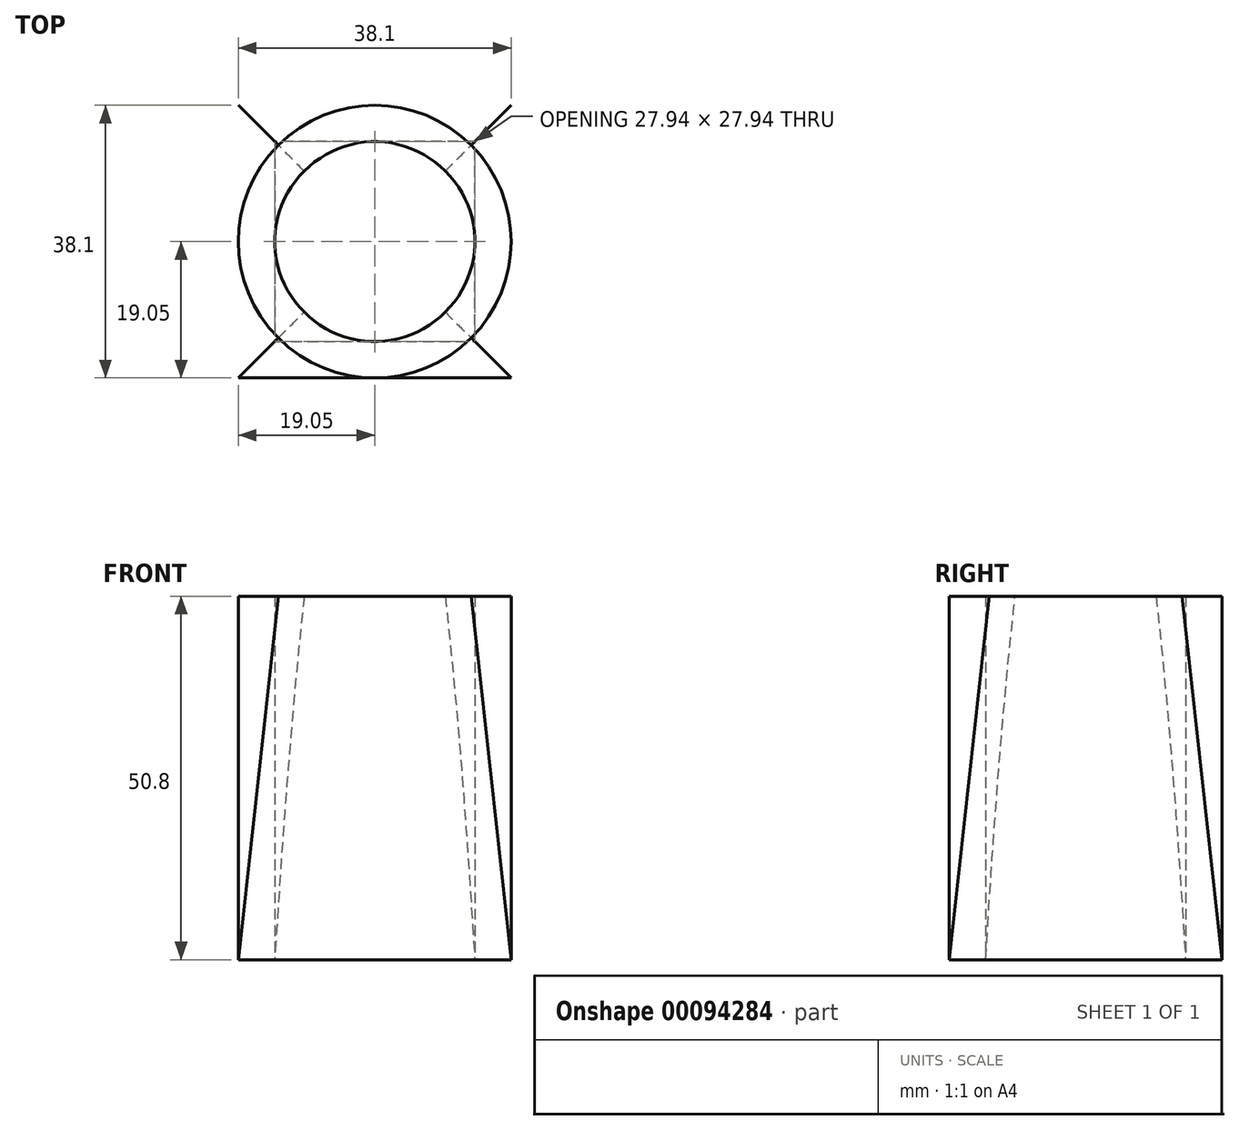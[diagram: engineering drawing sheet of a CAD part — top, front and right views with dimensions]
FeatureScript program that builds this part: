
annotation { "Feature Type Name" : "Feature", "Feature Type Description" : "" }
export const myFeature = defineFeature(function(context is Context, id is Id, definition is map)
    precondition{}
    {
        {
            var Q0;
            Q0=qCreatedBy(makeId("Front.planeOp"),FACE);
            var sketch = newSketch(context, id + "F0", { "sketchPlane" : qUnion([Q0])});
            skLineSegment(sketch, "E0", {"start": v(-19.05, 0) * mm, "end": v(-19.05, 50.8) * mm});
            skSolve(sketch);
        }
        {
            var Q0;
            Q0=qCreatedBy(makeId("Top.planeOp"),FACE);
            var sketch = newSketch(context, id + "F1", { "sketchPlane" : qUnion([Q0])});
            skLineSegment(sketch, "E1.bottom", {"start": v(-19.05, -19.05) * mm, "end": v(19.05, -19.05) * mm});
            skLineSegment(sketch, "E1.top", {"start": v(-19.05, 19.05) * mm, "end": v(19.05, 19.05) * mm});
            skLineSegment(sketch, "E1.left", {"start": v(-19.05, -19.05) * mm, "end": v(-19.05, 19.05) * mm});
            skLineSegment(sketch, "E1.right", {"start": v(19.05, -19.05) * mm, "end": v(19.05, 19.05) * mm});
            skPoint(sketch, "E1.middle", {"position": v(0, 0) * mm});
            skSolve(sketch);
        }
        {
            var Q0;
            Q0=sQuery(id+"F0.wireOp",VERTEX,"E0.end");
            var Q1;
            Q1=qCreatedBy(makeId("Top.planeOp"),FACE);
            cPlane(context, id + "F2", {"entities" : qUnion([Q0, Q1]), "cplaneType" : CPlaneType.PLANE_POINT, "offset" : 152.4 * mm, "width" : 152.4 * mm, "height" : 152.4 * mm});
        }
        {
            var Q0;
            Q0=qCreatedBy(id+"F2.planeOp",FACE);
            var sketch = newSketch(context, id + "F3", { "sketchPlane" : qUnion([Q0])});
            skCircle(sketch, "E2", {"center": v(0, 0) * mm, "radius": 19.05 * mm});
            skSolve(sketch);
        }
        {
            var Q0;
            Q0=makeQuery(id+"F1.imprint","IMPRINT",FACE,{"disambiguationData":[TD([[makeQuery(id+"F1.imprint","IMPRINT",EDGE,{"derivedFrom":sQuery(id+"F1.wireOp",EDGE,"E1.bottom")}),1.0]])]});
            var Q1;
            Q1=makeQuery(id+"F3.imprint","IMPRINT",FACE,{"disambiguationData":[TD([[makeQuery(id+"F3.imprint","IMPRINT",EDGE,{"derivedFrom":sQuery(id+"F3.wireOp",EDGE,"E2")}),1.0]])]});
            loft(context, id + "F4", {"sheetProfilesArray" : [{ "sheetProfileEntities" : qUnion([Q0]) }, { "sheetProfileEntities" : qUnion([Q1]) }]});
        }
        {
            var Q0;
            Q0=makeQuery(id+"F4.opLoft","CAP_FACE",FACE,{"disambiguationData":[OSD([makeQuery(id+"F3.imprint","IMPRINT",FACE,{"disambiguationData":[TD([[makeQuery(id+"F3.imprint","IMPRINT",EDGE,{"derivedFrom":sQuery(id+"F3.wireOp",EDGE,"E2")}),1.0]])]})])],"isStart":true});
            var Q1;
            Q1=makeQuery(id+"F4.opLoft","CAP_FACE",FACE,{"disambiguationData":[OSD([makeQuery(id+"F1.imprint","IMPRINT",FACE,{"disambiguationData":[TD([[makeQuery(id+"F1.imprint","IMPRINT",EDGE,{"derivedFrom":sQuery(id+"F1.wireOp",EDGE,"E1.bottom")}),1.0]])]})])],"isStart":true});
            shell(context, id + "F5", {"entities" : qUnion([Q0, Q1]), "thickness" : 5.08 * mm});
        }
    });
